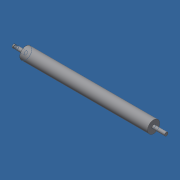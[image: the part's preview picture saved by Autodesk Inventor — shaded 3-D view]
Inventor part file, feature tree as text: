
AUTODESK INVENTOR PART (.ipt)
format: ipt  version: 2021 (Build 250183000, 183)  size: 94,720 bytes
history: native  units: in
note: dims shown in document units (in); Inventor stores cm internally (conversion verified against a paired STEP export)
features: extrude x5, sketch x5
ambient origin geometry x8: Origin, YZ Plane, XZ Plane, XY Plane, X Axis, Y Axis, Z Axis, Center Point
bodies: Solid1 (feature_tree)
feature tree (10):
  extrude  "Extrusion1"  Depth=8.7402in TaperAngle=0.0deg
  extrude  "Extrusion2"  Depth=0.8661in TaperAngle=0.0deg
  extrude  "Extrusion3"  Depth=0.5906in TaperAngle=0.0deg
  extrude  "Extrusion4"  Depth=0.1575in TaperAngle=0.0deg
  extrude  "Extrusion5"  Depth=0.0787in TaperAngle=0.0deg
  sketch  "Sketch1"  dims[d0=0.8268in d1=8.7402in d2=0.0in]
  sketch  "Sketch2"  dims[d3=0.2362in d4=0.8661in d5=0.0in]
  sketch  "Sketch3"  dims[d6=0.2362in d7=0.5906in d8=0.0in]
  sketch  "Sketch4"  dims[d9=0.1575in d10=0.1575in d11=0.0in]
  sketch  "Sketch5"  dims[d12=0.2362in d13=0.0787in d14=0.0in]
